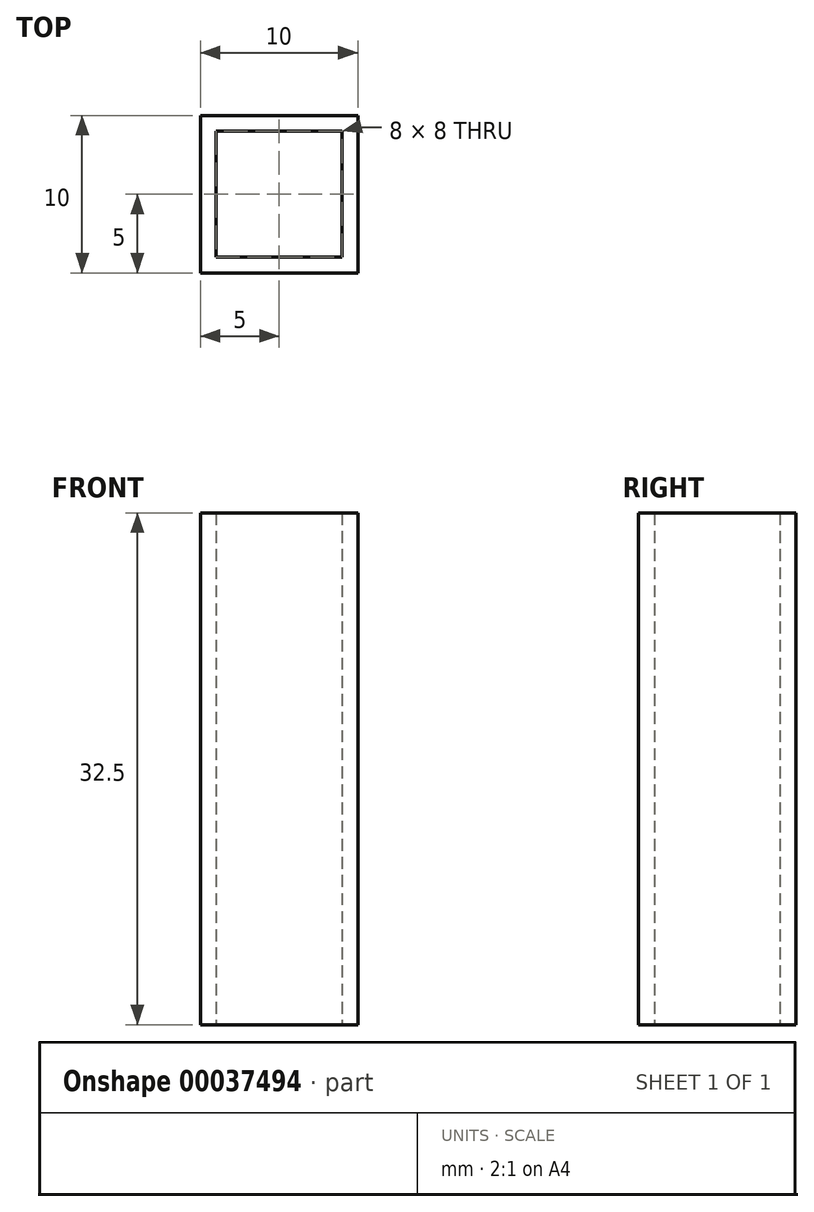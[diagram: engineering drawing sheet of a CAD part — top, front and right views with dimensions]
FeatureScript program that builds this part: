
annotation { "Feature Type Name" : "Feature", "Feature Type Description" : "" }
export const myFeature = defineFeature(function(context is Context, id is Id, definition is map)
    precondition{}
    {
        {
            var Q0;
            Q0=qCreatedBy(makeId("Top.planeOp"),FACE);
            var sketch = newSketch(context, id + "F0", { "sketchPlane" : qUnion([Q0])});
            skLineSegment(sketch, "E0.rect.bottom", {"start": v(5, -5) * mm, "end": v(-5, -5) * mm});
            skLineSegment(sketch, "E0.rect.top", {"start": v(5, 5) * mm, "end": v(-5, 5) * mm});
            skLineSegment(sketch, "E0.rect.left", {"start": v(5, -5) * mm, "end": v(5, 5) * mm});
            skLineSegment(sketch, "E0.rect.right", {"start": v(-5, -5) * mm, "end": v(-5, 5) * mm});
            skPoint(sketch, "E0.rect.middle", {"position": v(0, 0) * mm});
            skLineSegment(sketch, "E1.rect.bottom", {"start": v(4, -4) * mm, "end": v(-4, -4) * mm});
            skLineSegment(sketch, "E1.rect.top", {"start": v(4, 4) * mm, "end": v(-4, 4) * mm});
            skLineSegment(sketch, "E1.rect.left", {"start": v(4, -4) * mm, "end": v(4, 4) * mm});
            skLineSegment(sketch, "E1.rect.right", {"start": v(-4, -4) * mm, "end": v(-4, 4) * mm});
            skSolve(sketch);
        }
        {
            var Q0;
            Q0 = qSketchRegion(id + "F0", true);
            extrude(context, id + "F1", {"entities" : qUnion([Q0]), "depth" : 32.5 * mm});
        }
    });
